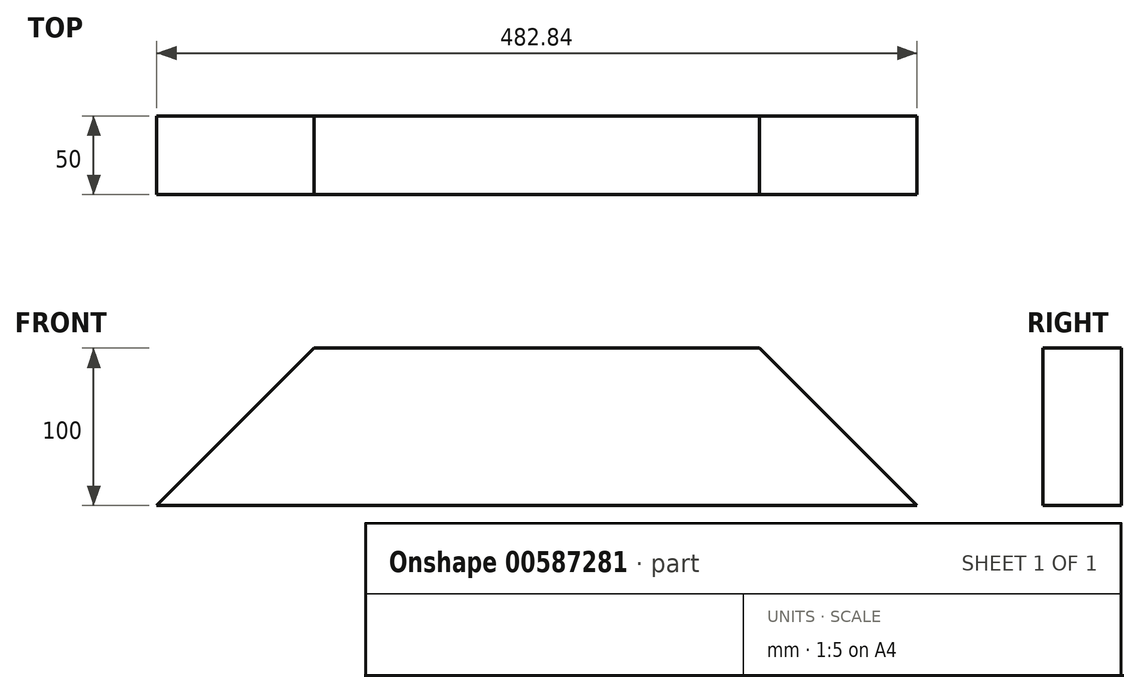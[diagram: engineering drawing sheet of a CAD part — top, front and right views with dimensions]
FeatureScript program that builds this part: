
annotation { "Feature Type Name" : "Feature", "Feature Type Description" : "" }
export const myFeature = defineFeature(function(context is Context, id is Id, definition is map)
    precondition{}
    {
        {
            var Q0;
            Q0=qCreatedBy(makeId("Front.planeOp"),FACE);
            var sketch = newSketch(context, id + "F0", { "sketchPlane" : qUnion([Q0])});
            skLineSegment(sketch, "E0", {"start": v(-1250, 0) * mm, "end": v(1250, 0) * mm, "construction": true});
            skLineSegment(sketch, "E1", {"start": v(1250, 0) * mm, "end": v(0, 1250) * mm, "construction": true});
            skLineSegment(sketch, "E2", {"start": v(0, 1250) * mm, "end": v(-1250, 0) * mm, "construction": true});
            skLineSegment(sketch, "E3", {"start": v(0, 1250) * mm, "end": v(-141.42, 1250) * mm, "construction": true});
            skLineSegment(sketch, "E4", {"start": v(-1250, 0) * mm, "end": v(-1391.42, 0) * mm, "construction": true});
            skLineSegment(sketch, "E5", {"start": v(-1391.42, 0) * mm, "end": v(-141.42, 1250) * mm, "construction": true});
            skLineSegment(sketch, "E6", {"start": v(-141.42, 1250) * mm, "end": v(141.42, 1250) * mm});
            skLineSegment(sketch, "E7", {"start": v(-141.42, 1250) * mm, "end": v(-241.42, 1150) * mm});
            skLineSegment(sketch, "E8", {"start": v(-241.42, 1150) * mm, "end": v(241.42, 1150) * mm});
            skLineSegment(sketch, "E9", {"start": v(241.42, 1150) * mm, "end": v(141.42, 1250) * mm});
            skPoint(sketch, "E10", {"position": v(0, 1150) * mm});
            skPoint(sketch, "E11", {"position": v(0, 1250) * mm});
            skSolve(sketch);
        }
        {
            var Q0;
            Q0=makeQuery(id+"F0.imprint","IMPRINT",FACE,{"disambiguationData":[TD([[makeQuery(id+"F0.imprint","IMPRINT",EDGE,{"derivedFrom":sQuery(id+"F0.wireOp",EDGE,"E6")}),-1.0]])]});
            extrude(context, id + "F1", {"entities" : qUnion([Q0]), "depth" : 50 * mm, "offsetDistance" : 25 * mm});
        }
    });
